# Revit family: PLM-SNK-AEC-Wash_Basin
name_source: partatom
category: Plumbing Fixtures
revit_build: Autodesk Revit 2016 (Build: 20150220_1215(x64)
units: mm (PartAtom-declared; Revit-internal decimal feet)

## family parameters
Always vertical = Yes
Cut with Voids When Loaded = No
Part Type = Normal
Room Calculation Point = No
Round Connector Dimension = Use Diameter
Shared = No
Work Plane-Based = No

## types (1)
- Standard
    Drain Connection Diameter = 12 mm  [stored 0.0393701 ft]
    Nominal Diameter = 12 mm
    Shelf Depth = 300 mm
    Shelf Length = 875 mm  [stored 2.87073 ft]
    Shelf Material = Wood - Walnut Natural
    Shelf Thickness = 30 mm  [stored 0.0984252 ft]
    Show Yellow Background = Yes
    Sink Material = Porcelain
    Tap Height = 300 mm
    Taps and Fittings Material = Metal - Chrome Polished

note: [stored X ft] marks values corroborated as IEEE doubles in the binary element streams (Revit-internal decimal feet)

## geometry (parser evidence)
native form markers: Sweep x9
no freeform markers — native parametric forms only
